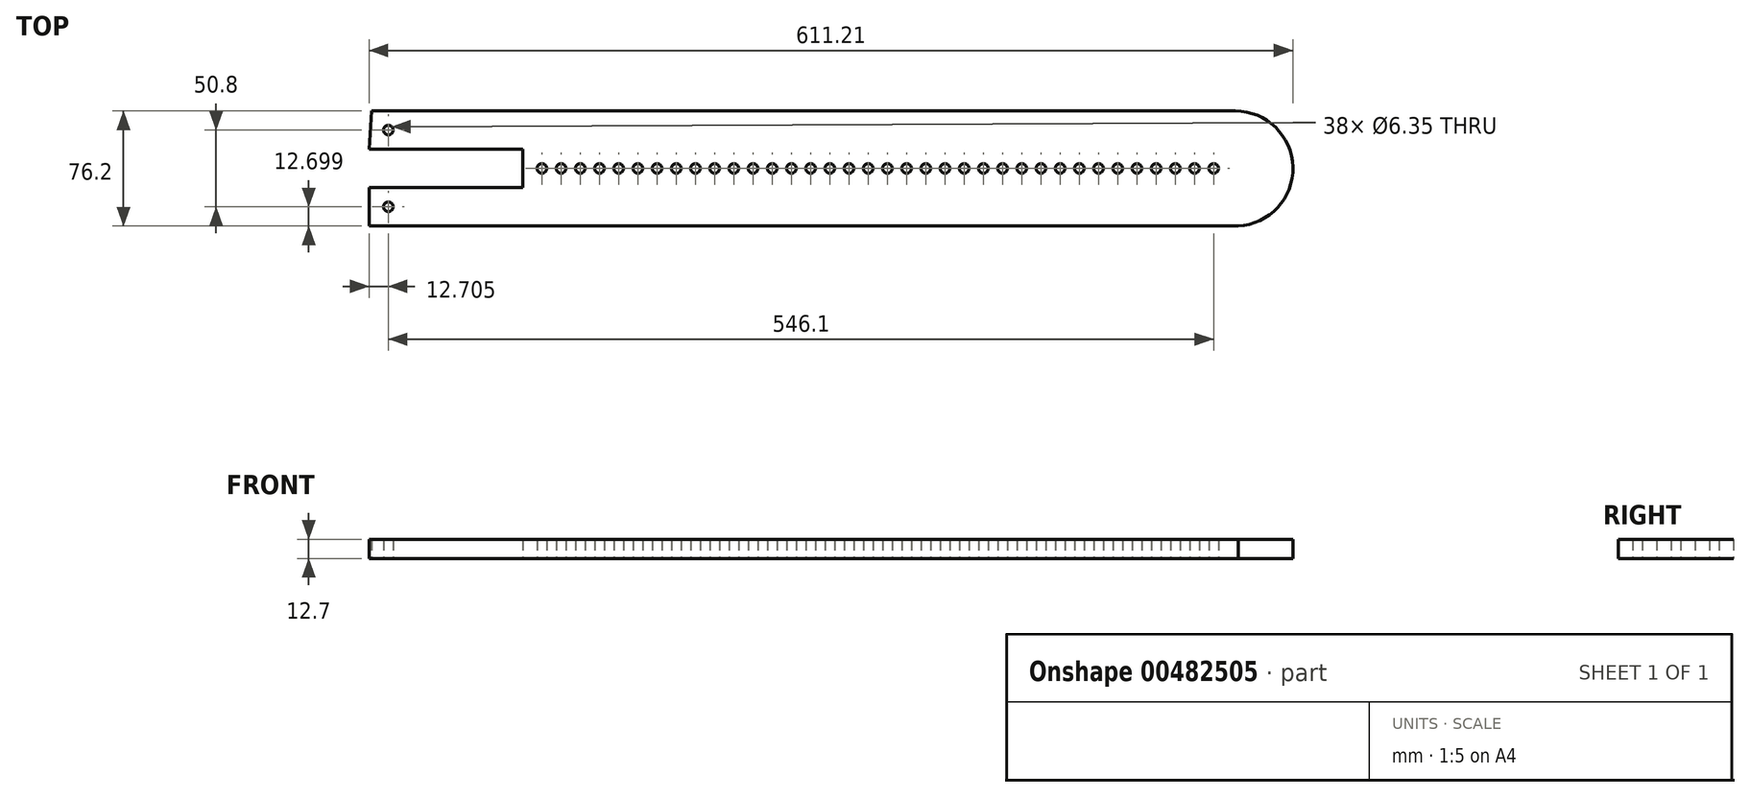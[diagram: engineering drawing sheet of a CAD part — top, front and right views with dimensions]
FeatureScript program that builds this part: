
annotation { "Feature Type Name" : "Feature", "Feature Type Description" : "" }
export const myFeature = defineFeature(function(context is Context, id is Id, definition is map)
    precondition{}
    {
        {
            var Q0;
            Q0=qCreatedBy(makeId("Top.planeOp"),FACE);
            var sketch = newSketch(context, id + "F0", { "sketchPlane" : qUnion([Q0])});
            skCircle(sketch, "E0", {"center": v(259.84, -2.3) * mm, "radius": 38.1 * mm});
            skPoint(sketch, "E0.first.point", {"position": v(297.94, -2.25) * mm});
            skPoint(sketch, "E0.second.point", {"position": v(221.74, -2.25) * mm});
            skPoint(sketch, "E0.second.point.positionSnap0", {"position": v(297.94, -2.25) * mm});
            skPoint(sketch, "E0.third.point", {"position": v(261.68, -40.35) * mm});
            skPoint(sketch, "E1.middle", {"position": v(-313.27, -2.25) * mm});
            skLineSegment(sketch, "E2.bottom", {"start": v(-313.27, 10.45) * mm, "end": v(-211.67, 10.45) * mm});
            skLineSegment(sketch, "E2.top", {"start": v(-313.27, -14.95) * mm, "end": v(-211.67, -14.95) * mm});
            skLineSegment(sketch, "E2.right", {"start": v(-211.67, 10.45) * mm, "end": v(-211.67, -14.95) * mm});
            skLineSegment(sketch, "E3", {"start": v(-311.66, 35.85) * mm, "end": v(-313.27, 10.45) * mm});
            skLineSegment(sketch, "E4", {"start": v(-313.27, -14.95) * mm, "end": v(-313.27, -40.35) * mm});
            skCircle(sketch, "E5", {"center": v(-300.57, -27.65) * mm, "radius": 3.18 * mm});
            skCircle(sketch, "E6", {"center": v(-300.57, 23.15) * mm, "radius": 3.18 * mm});
            skCircle(sketch, "E7", {"center": v(-198.97, -2.25) * mm, "radius": 3.18 * mm});
            skCircle(sketch, "E8.1.0.0", {"center": v(-186.27, -2.25) * mm, "radius": 3.18 * mm});
            skCircle(sketch, "E8.2.0.0", {"center": v(-173.57, -2.25) * mm, "radius": 3.18 * mm});
            skCircle(sketch, "E8.3.0.0", {"center": v(-160.87, -2.25) * mm, "radius": 3.18 * mm});
            skCircle(sketch, "E8.4.0.0", {"center": v(-148.17, -2.25) * mm, "radius": 3.18 * mm});
            skCircle(sketch, "E8.5.0.0", {"center": v(-135.47, -2.25) * mm, "radius": 3.18 * mm});
            skCircle(sketch, "E8.6.0.0", {"center": v(-122.77, -2.25) * mm, "radius": 3.18 * mm});
            skCircle(sketch, "E8.7.0.0", {"center": v(-110.07, -2.25) * mm, "radius": 3.18 * mm});
            skCircle(sketch, "E8.8.0.0", {"center": v(-97.37, -2.25) * mm, "radius": 3.18 * mm});
            skCircle(sketch, "E8.9.0.0", {"center": v(-84.67, -2.25) * mm, "radius": 3.18 * mm});
            skCircle(sketch, "E8.10.0.0", {"center": v(-71.97, -2.25) * mm, "radius": 3.18 * mm});
            skCircle(sketch, "E8.11.0.0", {"center": v(-59.27, -2.25) * mm, "radius": 3.18 * mm});
            skCircle(sketch, "E8.12.0.0", {"center": v(-46.57, -2.25) * mm, "radius": 3.18 * mm});
            skCircle(sketch, "E8.13.0.0", {"center": v(-33.87, -2.25) * mm, "radius": 3.18 * mm});
            skCircle(sketch, "E8.14.0.0", {"center": v(-21.17, -2.25) * mm, "radius": 3.18 * mm});
            skCircle(sketch, "E8.15.0.0", {"center": v(-8.47, -2.25) * mm, "radius": 3.18 * mm});
            skCircle(sketch, "E8.16.0.0", {"center": v(4.23, -2.25) * mm, "radius": 3.18 * mm});
            skCircle(sketch, "E8.17.0.0", {"center": v(16.93, -2.25) * mm, "radius": 3.18 * mm});
            skCircle(sketch, "E8.18.0.0", {"center": v(29.63, -2.25) * mm, "radius": 3.18 * mm});
            skCircle(sketch, "E8.19.0.0", {"center": v(42.33, -2.25) * mm, "radius": 3.18 * mm});
            skLineSegment(sketch, "E8.direction1", {"start": v(-198.97, -2.25) * mm, "end": v(-186.27, -2.25) * mm, "construction": true});
            skCircle(sketch, "E9.0.20.0", {"center": v(55.03, -2.25) * mm, "radius": 3.18 * mm});
            skCircle(sketch, "E9.0.21.0", {"center": v(67.73, -2.25) * mm, "radius": 3.18 * mm});
            skCircle(sketch, "E9.0.22.0", {"center": v(80.43, -2.25) * mm, "radius": 3.18 * mm});
            skCircle(sketch, "E9.0.23.0", {"center": v(93.13, -2.25) * mm, "radius": 3.18 * mm});
            skCircle(sketch, "E9.0.24.0", {"center": v(105.83, -2.25) * mm, "radius": 3.18 * mm});
            skCircle(sketch, "E9.0.25.0", {"center": v(118.53, -2.25) * mm, "radius": 3.18 * mm});
            skCircle(sketch, "E9.0.26.0", {"center": v(131.23, -2.25) * mm, "radius": 3.18 * mm});
            skCircle(sketch, "E9.0.27.0", {"center": v(143.93, -2.25) * mm, "radius": 3.18 * mm});
            skCircle(sketch, "E9.0.28.0", {"center": v(156.63, -2.25) * mm, "radius": 3.18 * mm});
            skCircle(sketch, "E9.0.29.0", {"center": v(169.33, -2.25) * mm, "radius": 3.18 * mm});
            skCircle(sketch, "E10.0.30.0", {"center": v(182.03, -2.25) * mm, "radius": 3.18 * mm});
            skCircle(sketch, "E10.0.31.0", {"center": v(194.73, -2.25) * mm, "radius": 3.18 * mm});
            skCircle(sketch, "E10.0.32.0", {"center": v(207.43, -2.25) * mm, "radius": 3.18 * mm});
            skCircle(sketch, "E11.0.33.0", {"center": v(220.13, -2.25) * mm, "radius": 3.18 * mm});
            skCircle(sketch, "E11.0.34.0", {"center": v(232.83, -2.25) * mm, "radius": 3.18 * mm});
            skCircle(sketch, "E11.0.35.0", {"center": v(245.53, -2.25) * mm, "radius": 3.18 * mm});
            skLineSegment(sketch, "E12", {"start": v(-311.66, 35.85) * mm, "end": v(259.84, 35.8) * mm});
            skLineSegment(sketch, "E13", {"start": v(-313.27, -40.35) * mm, "end": v(261.68, -40.35) * mm});
            skSolve(sketch);
        }
        {
            var Q0;
            Q0=makeQuery(id+"F0.imprint","IMPRINT",FACE,{"disambiguationData":[TD([[makeQuery(id+"F0.imprint","IMPRINT",EDGE,{"derivedFrom":sQuery(id+"F0.wireOp",EDGE,"E2.bottom")}),1.0]])]});
            var Q1;
            Q1=makeQuery(id+"F0.imprint","IMPRINT",FACE,{"disambiguationData":[TD([[makeQuery(id+"F0.imprint","IMPRINT",EDGE,{"derivedFrom":sQuery(id+"F0.wireOp",EDGE,"E11.0.34.0")}),-1.0]])]});
            extrude(context, id + "F1", {"entities" : qUnion([Q0, Q1]), "depth" : 12.7 * mm});
        }
    });
